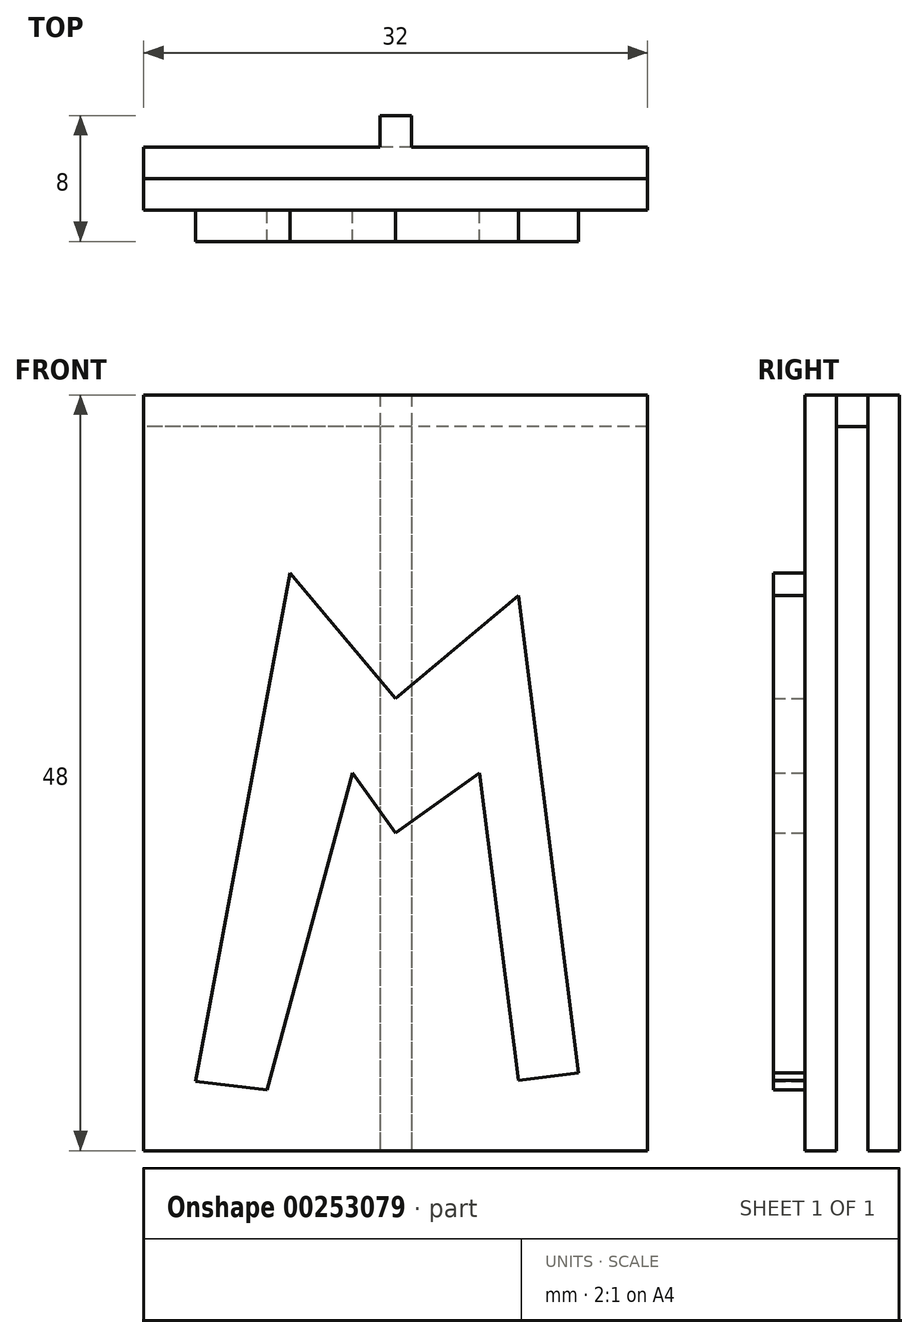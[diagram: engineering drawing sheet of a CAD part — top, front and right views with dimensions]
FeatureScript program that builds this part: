
annotation { "Feature Type Name" : "Feature", "Feature Type Description" : "" }
export const myFeature = defineFeature(function(context is Context, id is Id, definition is map)
    precondition{}
    {
        {
            var Q0;
            Q0=qCreatedBy(makeId("Front.planeOp"),FACE);
            var sketch = newSketch(context, id + "F0", { "sketchPlane" : qUnion([Q0])});
            skLineSegment(sketch, "E0.bottom", {"start": v(-1, 24) * mm, "end": v(1, 24) * mm});
            skLineSegment(sketch, "E0.top", {"start": v(-1, -24) * mm, "end": v(1, -24) * mm});
            skLineSegment(sketch, "E0.left", {"start": v(-1, 24) * mm, "end": v(-1, -24) * mm});
            skLineSegment(sketch, "E0.right", {"start": v(1, 24) * mm, "end": v(1, -24) * mm});
            skPoint(sketch, "E0.middle", {"position": v(0, 0) * mm});
            skSolve(sketch);
        }
        {
            var Q0;
            Q0 = qSketchRegion(id + "F0", true);
            extrude(context, id + "F1", {"entities" : qUnion([Q0]), "depth" : 2 * mm});
        }
        {
            var Q0;
            Q0=makeQuery(id+"F1.opExtrude","CAP_FACE",FACE,{"disambiguationData":[OSD([sQuery(id+"F0.wireOp",EDGE,"E0.bottom"),sQuery(id+"F0.wireOp",EDGE,"E0.top"),sQuery(id+"F0.wireOp",EDGE,"E0.left"),sQuery(id+"F0.wireOp",EDGE,"E0.right")])],"isStart":false});
            var sketch = newSketch(context, id + "F2", { "sketchPlane" : qUnion([Q0])});
            skLineSegment(sketch, "E1", {"start": v(-1, 24) * mm, "end": v(-16, 24) * mm});
            skLineSegment(sketch, "E2", {"start": v(-1, 24) * mm, "end": v(16, 24) * mm});
            skLineSegment(sketch, "E3", {"start": v(-16, 24) * mm, "end": v(-16, 22) * mm});
            skLineSegment(sketch, "E4", {"start": v(16, 24) * mm, "end": v(16, 22) * mm});
            skLineSegment(sketch, "E5", {"start": v(16, 22) * mm, "end": v(-16, 22) * mm});
            skSolve(sketch);
        }
        {
            var Q0;
            Q0 = qSketchRegion(id + "F2", true);
            extrude(context, id + "F3", {"entities" : qUnion([Q0]), "operationType" : NewBodyOperationType.ADD, "depth" : 2 * mm});
        }
        {
            var Q0;
            Q0=makeQuery(id+"F3.opExtrude","SWEPT_FACE",FACE,{"disambiguationData":[OSD([sQuery(id+"F2.wireOp",EDGE,"E3")])]});
            var sketch = newSketch(context, id + "F4", { "sketchPlane" : qUnion([Q0])});
            skLineSegment(sketch, "E6", {"start": v(4, 24) * mm, "end": v(6, 24) * mm});
            skLineSegment(sketch, "E7", {"start": v(6, 24) * mm, "end": v(6, -24) * mm});
            skLineSegment(sketch, "E8", {"start": v(6, -24) * mm, "end": v(4, -24) * mm});
            skLineSegment(sketch, "E9", {"start": v(4, -24) * mm, "end": v(4, 24) * mm});
            skSolve(sketch);
        }
        {
            var Q0;
            Q0 = qSketchRegion(id + "F4", true);
            extrude(context, id + "F5", {"entities" : qUnion([Q0]), "oppositeDirection" : true, "depth" : 32 * mm});
        }
        {
            var Q0;
            Q0=makeQuery(id+"F5.opExtrude","SWEPT_FACE",FACE,{"disambiguationData":[OSD([sQuery(id+"F4.wireOp",EDGE,"E7")])]});
            var sketch = newSketch(context, id + "F6", { "sketchPlane" : qUnion([Q0])});
            skLineSegment(sketch, "E10", {"start": v(-12.7, -19.6) * mm, "end": v(-6.71, 12.7) * mm});
            skLineSegment(sketch, "E11", {"start": v(-6.71, 12.7) * mm, "end": v(0, 4.72) * mm});
            skLineSegment(sketch, "E12", {"start": v(0, 4.72) * mm, "end": v(7.8, 11.27) * mm});
            skLineSegment(sketch, "E13", {"start": v(7.8, 11.27) * mm, "end": v(11.61, -19.05) * mm});
            skLineSegment(sketch, "E14", {"start": v(11.61, -19.05) * mm, "end": v(7.8, -19.53) * mm});
            skLineSegment(sketch, "E15", {"start": v(7.8, -19.53) * mm, "end": v(5.33, 0) * mm});
            skLineSegment(sketch, "E16", {"start": v(5.33, 0) * mm, "end": v(0, -3.81) * mm});
            skLineSegment(sketch, "E17", {"start": v(0, -3.81) * mm, "end": v(-2.72, 0) * mm});
            skLineSegment(sketch, "E18", {"start": v(-2.72, 0) * mm, "end": v(-8.17, -20.14) * mm});
            skLineSegment(sketch, "E19", {"start": v(-8.17, -20.14) * mm, "end": v(-12.7, -19.6) * mm});
            skSolve(sketch);
        }
        {
            var Q0;
            Q0 = qSketchRegion(id + "F6", true);
            extrude(context, id + "F7", {"entities" : qUnion([Q0]), "depth" : 2 * mm});
        }
    });
